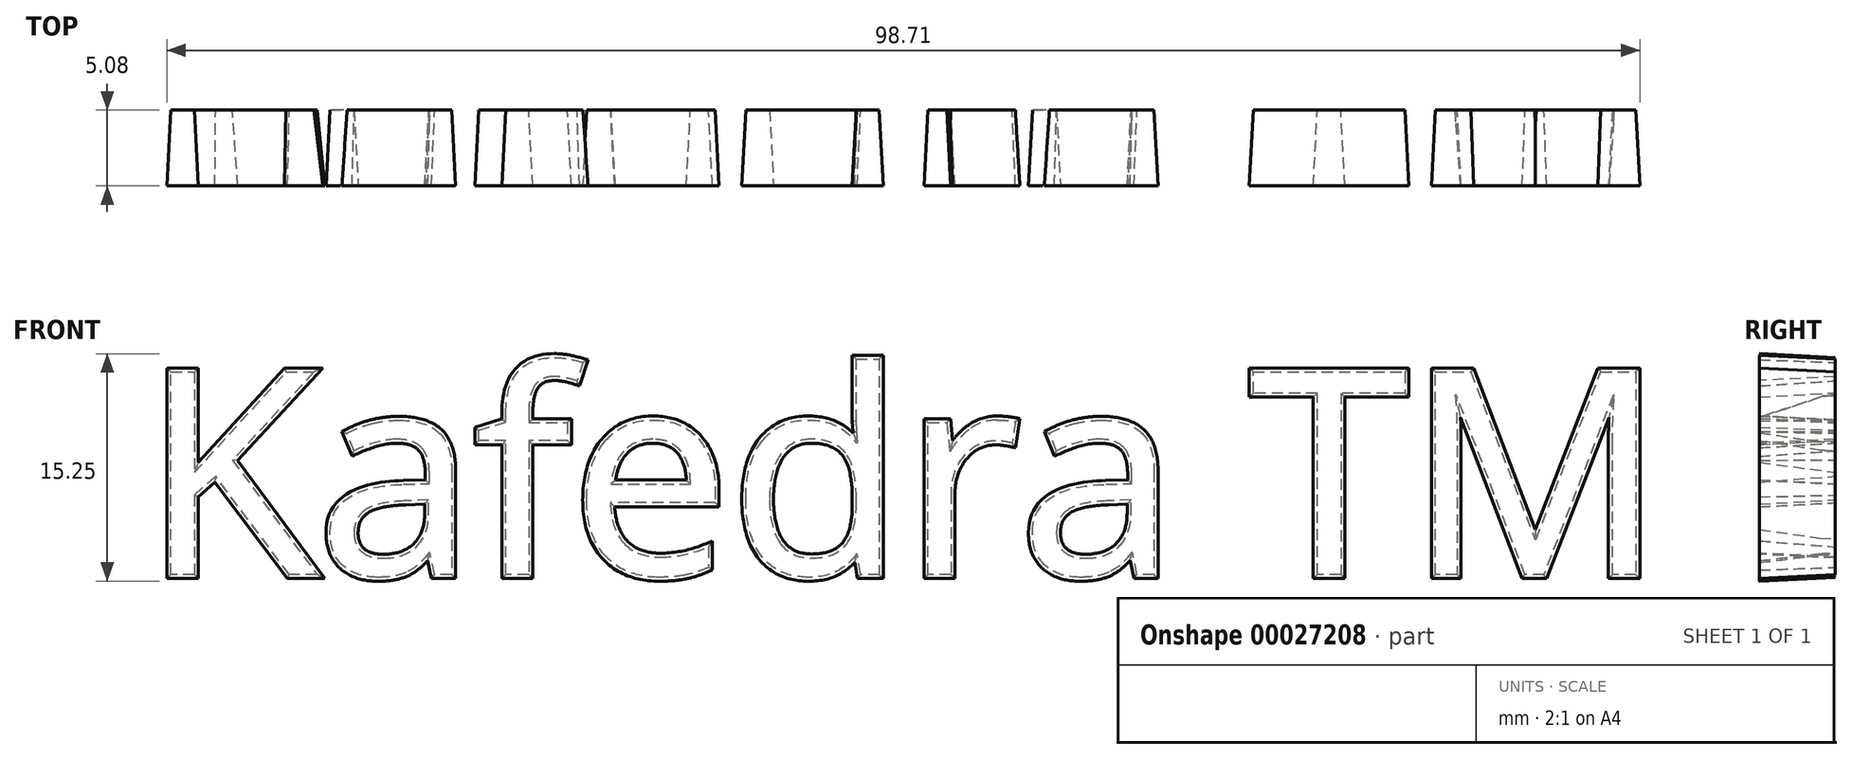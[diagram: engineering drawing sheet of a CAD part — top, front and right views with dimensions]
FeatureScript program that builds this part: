
annotation { "Feature Type Name" : "Feature", "Feature Type Description" : "" }
export const myFeature = defineFeature(function(context is Context, id is Id, definition is map)
    precondition{}
    {
        {
            var Q0;
            Q0=qCreatedBy(makeId("Front.planeOp"),FACE);
            var sketch = newSketch(context, id + "F0", { "sketchPlane" : qUnion([Q0])});
            skText(sketch, "E0", { "text": "Kafedra TM", "fontName": "OpenSans-Regular.ttf"});
            const initialGuessF0  = {"E0": [-0.03583, 0, 1, 0, 0.01368]};
            skSetInitialGuess(sketch, initialGuessF0);
            skSolve(sketch);
        }
        {
            var Q0;
            Q0 = qSketchRegion(id + "F0", true);
            extrude(context, id + "F1", {"entities" : qUnion([Q0]), "depth" : 5.08 * mm, "hasDraft" : true, "draftAngle" : 3 * degree});
        }
    });
